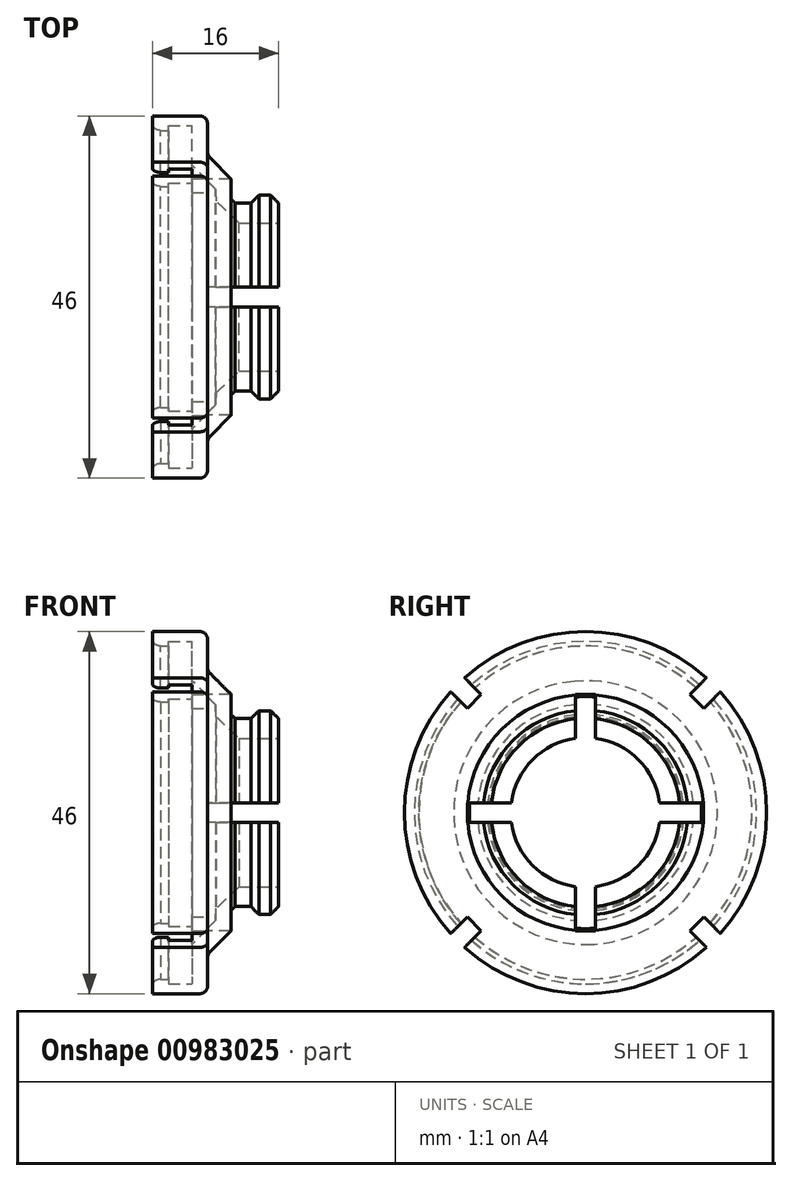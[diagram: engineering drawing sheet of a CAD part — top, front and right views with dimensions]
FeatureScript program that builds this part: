
annotation { "Feature Type Name" : "Feature", "Feature Type Description" : "" }
export const myFeature = defineFeature(function(context is Context, id is Id, definition is map)
    precondition{}
    {
        {
            var Q0;
            Q0=qCreatedBy(makeId("Front.planeOp"),FACE);
            var sketch = newSketch(context, id + "F0", { "sketchPlane" : qUnion([Q0])});
            skLineSegment(sketch, "E0", {"start": v(0, 0) * mm, "end": v(-33.83, 0) * mm, "construction": true});
            skLineSegment(sketch, "E1", {"start": v(-7, 21.75) * mm, "end": v(-5, 21.75) * mm});
            skLineSegment(sketch, "E2", {"start": v(-5, 21.75) * mm, "end": v(-5, 21.75) * mm});
            skLineSegment(sketch, "E3", {"start": v(-5, 21.75) * mm, "end": v(-2, 21.75) * mm});
            skLineSegment(sketch, "E4", {"start": v(5.5, 12) * mm, "end": v(5.5, 13) * mm});
            skLineSegment(sketch, "E5", {"start": v(-2, 21.75) * mm, "end": v(-2, 16.75) * mm});
            skLineSegment(sketch, "E6", {"start": v(-2, 16.75) * mm, "end": v(1, 13.75) * mm});
            skLineSegment(sketch, "E7", {"start": v(3, 15) * mm, "end": v(0, 18) * mm});
            skLineSegment(sketch, "E8", {"start": v(0, 18) * mm, "end": v(0, 23) * mm});
            skLineSegment(sketch, "E9", {"start": v(-7, 23) * mm, "end": v(-7, 21.75) * mm});
            skLineSegment(sketch, "E10", {"start": v(9, 9.5) * mm, "end": v(4, 9.5) * mm});
            skLineSegment(sketch, "E11", {"start": v(1.06, 12.25) * mm, "end": v(1, 13.75) * mm});
            skArc(sketch, "E12", {"start": v(-7, 21.75) * mm, "mid": v(-6, 21.17) * mm, "end": v(-5, 21.75) * mm});
            skLineSegment(sketch, "E13", {"start": v(-7, 23) * mm, "end": v(0, 23) * mm});
            skLineSegment(sketch, "E14", {"start": v(1.06, 12.25) * mm, "end": v(4, 9.5) * mm});
            skLineSegment(sketch, "E15.bottom", {"start": v(-6, 21.75) * mm, "end": v(-5, 21.75) * mm});
            skLineSegment(sketch, "E15.top", {"start": v(-6, 21.17) * mm, "end": v(-5, 21.17) * mm});
            skLineSegment(sketch, "E15.left", {"start": v(-6, 21.75) * mm, "end": v(-6, 21.17) * mm});
            skLineSegment(sketch, "E15.right", {"start": v(-5, 21.75) * mm, "end": v(-5, 21.17) * mm});
            skLineSegment(sketch, "E16", {"start": v(5.5, 13) * mm, "end": v(9, 13) * mm});
            skLineSegment(sketch, "E17", {"start": v(5.5, 12) * mm, "end": v(3.5, 12) * mm});
            skLineSegment(sketch, "E18", {"start": v(3, 15) * mm, "end": v(3, 12.5) * mm});
            skLineSegment(sketch, "E19", {"start": v(3, 12.5) * mm, "end": v(3.5, 12) * mm});
            skLineSegment(sketch, "E20", {"start": v(9, 13) * mm, "end": v(9, 9.5) * mm});
            skSolve(sketch);
        }
        {
            var Q0;
            Q0=qCreatedBy(makeId("Right.planeOp"),FACE);
            var sketch = newSketch(context, id + "F1", { "sketchPlane" : qUnion([Q0])});
            skLineSegment(sketch, "E21.bottom", {"start": v(-1.25, 15) * mm, "end": v(1.25, 15) * mm});
            skLineSegment(sketch, "E21.top", {"start": v(-1.25, -15) * mm, "end": v(1.25, -15) * mm});
            skLineSegment(sketch, "E21.left", {"start": v(-1.25, 15) * mm, "end": v(-1.25, -15) * mm});
            skLineSegment(sketch, "E21.right", {"start": v(1.25, 15) * mm, "end": v(1.25, -15) * mm});
            skSolve(sketch);
        }
        {
            var Q0;
            Q0=qCreatedBy(makeId("Right.planeOp"),FACE);
            var sketch = newSketch(context, id + "F2", { "sketchPlane" : qUnion([Q0])});
            skLineSegment(sketch, "E22.bottom", {"start": v(-15, 1.25) * mm, "end": v(15, 1.25) * mm});
            skLineSegment(sketch, "E22.top", {"start": v(-15, -1.25) * mm, "end": v(15, -1.25) * mm});
            skLineSegment(sketch, "E22.left", {"start": v(-15, 1.25) * mm, "end": v(-15, -1.25) * mm});
            skLineSegment(sketch, "E22.right", {"start": v(15, 1.25) * mm, "end": v(15, -1.25) * mm});
            skSolve(sketch);
        }
        {
            var Q0;
            Q0 = qSketchRegion(id + "F0", true);
            var Q1;
            Q1=sQuery(id+"F0.wireOp",EDGE,"E0");
            revolve(context, id + "F3", {"surfaceOperationType" : NewSurfaceOperationType.NEW, "entities" : qUnion([Q0]), "axis" : qUnion([Q1]), "revolveType" : RevolveType.FULL});
        }
        {
            var Q0;
            Q0 = qSketchRegion(id + "F1", true);
            extrude(context, id + "F4", {"entities" : qUnion([Q0]), "operationType" : NewBodyOperationType.REMOVE, "depth" : 20 * mm, "offsetDistance" : 25 * mm});
        }
        {
            var Q0;
            Q0 = qSketchRegion(id + "F2", true);
            extrude(context, id + "F5", {"entities" : qUnion([Q0]), "operationType" : NewBodyOperationType.REMOVE, "depth" : 20 * mm, "offsetDistance" : 25 * mm});
        }
        {
            var Q0;
            Q0=makeQuery(id+"F3.opRevolve","SWEPT_EDGE",EDGE,{"disambiguationData":[OSD([sQuery(id+"F0.wireOp",EDGE,"AhvpBqBA-tZ8w-fHzy-bnX2-0eLYJSzQ2YSn"),sQuery(id+"F0.wireOp",EDGE,"E8")])]});
            fillet(context, id + "F6", {"entities" : qUnion([Q0]), "radius" : 1 * mm, "tangentPropagation" : true, "allowEdgeOverflow" : false});
        }
        {
            var Q0;
            Q0=qCreatedBy(makeId("Right.planeOp"),FACE);
            var sketch = newSketch(context, id + "F7", { "sketchPlane" : qUnion([Q0])});
            skLineSegment(sketch, "E23.bottom", {"start": v(-16.8, 18.56) * mm, "end": v(-13.26, 15.03) * mm});
            skLineSegment(sketch, "E23.top", {"start": v(-18.56, 16.8) * mm, "end": v(-15.03, 13.26) * mm});
            skLineSegment(sketch, "E23.left", {"start": v(-16.8, 18.56) * mm, "end": v(-18.56, 16.8) * mm});
            skLineSegment(sketch, "E23.right", {"start": v(-13.26, 15.03) * mm, "end": v(-15.03, 13.26) * mm});
            skPoint(sketch, "E23.middle", {"position": v(-22.5, 0) * mm});
            skLineSegment(sketch, "E24.0", {"start": v(-16.8, 18.56) * mm, "end": v(-13.26, 15.03) * mm, "construction": true});
            skLineSegment(sketch, "E24.1", {"start": v(-16.8, 18.56) * mm, "end": v(-16.8, 18.56) * mm});
            skLineSegment(sketch, "E24.8", {"start": v(-18.56, 16.8) * mm, "end": v(-18.56, 16.8) * mm});
            skLineSegment(sketch, "E24.9", {"start": v(-18.56, 16.8) * mm, "end": v(-16.8, 18.56) * mm, "construction": true});
            skLineSegment(sketch, "E25.1.0", {"start": v(16.8, 18.56) * mm, "end": v(13.26, 15.03) * mm});
            skLineSegment(sketch, "E25.1.1", {"start": v(15.03, 13.26) * mm, "end": v(13.26, 15.03) * mm});
            skLineSegment(sketch, "E25.1.2", {"start": v(18.56, 16.8) * mm, "end": v(15.03, 13.26) * mm});
            skLineSegment(sketch, "E25.1.3", {"start": v(16.8, 18.56) * mm, "end": v(18.56, 16.8) * mm});
            skLineSegment(sketch, "E25.2.0", {"start": v(18.56, -16.8) * mm, "end": v(15.03, -13.26) * mm});
            skLineSegment(sketch, "E25.2.1", {"start": v(13.26, -15.03) * mm, "end": v(15.03, -13.26) * mm});
            skLineSegment(sketch, "E25.2.2", {"start": v(16.8, -18.56) * mm, "end": v(13.26, -15.03) * mm});
            skLineSegment(sketch, "E25.2.3", {"start": v(18.56, -16.8) * mm, "end": v(16.8, -18.56) * mm});
            skLineSegment(sketch, "E25.3.0", {"start": v(-16.8, -18.56) * mm, "end": v(-13.26, -15.03) * mm});
            skLineSegment(sketch, "E25.3.1", {"start": v(-15.03, -13.26) * mm, "end": v(-13.26, -15.03) * mm});
            skLineSegment(sketch, "E25.3.2", {"start": v(-18.56, -16.8) * mm, "end": v(-15.03, -13.26) * mm});
            skLineSegment(sketch, "E25.3.3", {"start": v(-16.8, -18.56) * mm, "end": v(-18.56, -16.8) * mm});
            skPoint(sketch, "E25.center", {"position": v(0, 0) * mm});
            skLineSegment(sketch, "E25.anchor1", {"start": v(0, 0) * mm, "end": v(-15.03, 13.26) * mm, "construction": true});
            skLineSegment(sketch, "E25.anchor2", {"start": v(0, 0) * mm, "end": v(-13.26, -15.03) * mm, "construction": true});
            skLineSegment(sketch, "E26", {"start": v(-13.26, -15.03) * mm, "end": v(-15.03, -13.26) * mm});
            skLineSegment(sketch, "E27", {"start": v(-18.56, -16.8) * mm, "end": v(-16.8, -18.56) * mm});
            skSolve(sketch);
        }
        {
            var Q0;
            Q0=makeQuery(id+"F7.imprint","IMPRINT",FACE,{"disambiguationData":[TD([[makeQuery(id+"F7.imprint","IMPRINT",EDGE,{"derivedFrom":sQuery(id+"F7.wireOp",EDGE,"E23.bottom")}),-1.0]])]});
            var Q1;
            Q1=makeQuery(id+"F7.imprint","IMPRINT",FACE,{"disambiguationData":[TD([[makeQuery(id+"F7.imprint","IMPRINT",EDGE,{"derivedFrom":sQuery(id+"F7.wireOp",EDGE,"E25.1.0")}),1.0]])]});
            var Q2;
            Q2=makeQuery(id+"F7.imprint","IMPRINT",FACE,{"disambiguationData":[TD([[makeQuery(id+"F7.imprint","IMPRINT",EDGE,{"derivedFrom":sQuery(id+"F7.wireOp",EDGE,"E25.2.0")}),1.0]])]});
            var Q3;
            Q3=makeQuery(id+"F7.imprint","IMPRINT",FACE,{"disambiguationData":[TD([[makeQuery(id+"F7.imprint","IMPRINT",EDGE,{"derivedFrom":sQuery(id+"F7.wireOp",EDGE,"E25.3.0")}),1.0]])]});
            var Q4;
            Q4=sQuery(id+"F7.wireOp",EDGE,"E25.3.0");
            var Q5;
            Q5=sQuery(id+"F7.wireOp",EDGE,"E25.3.2");
            var Q6;
            Q6=sQuery(id+"F7.wireOp",EDGE,"E26");
            var Q7;
            Q7=sQuery(id+"F7.wireOp",EDGE,"E23.top");
            var Q8;
            Q8=sQuery(id+"F7.wireOp",EDGE,"E23.left");
            var Q9;
            Q9=sQuery(id+"F7.wireOp",EDGE,"E23.bottom");
            var Q10;
            Q10=sQuery(id+"F7.wireOp",EDGE,"E23.right");
            var Q11;
            Q11=sQuery(id+"F7.wireOp",EDGE,"E25.1.1");
            var Q12;
            Q12=sQuery(id+"F7.wireOp",EDGE,"E25.1.0");
            var Q13;
            Q13=sQuery(id+"F7.wireOp",EDGE,"E25.1.3");
            var Q14;
            Q14=sQuery(id+"F7.wireOp",EDGE,"E25.1.2");
            var Q15;
            Q15=sQuery(id+"F7.wireOp",EDGE,"E25.2.0");
            var Q16;
            Q16=sQuery(id+"F7.wireOp",EDGE,"E25.2.3");
            var Q17;
            Q17=sQuery(id+"F7.wireOp",EDGE,"E25.2.2");
            var Q18;
            Q18=sQuery(id+"F7.wireOp",EDGE,"E25.2.1");
            extrude(context, id + "F8", {"entities" : qUnion([Q0, Q1, Q2, Q3]), "operationType" : NewBodyOperationType.REMOVE, "surfaceEntities" : qUnion([Q4, Q5, Q6, Q7, Q8, Q9, Q10, Q11, Q12, Q13, Q14, Q15, Q16, Q17, Q18]), "oppositeDirection" : true, "depth" : 13.7 * mm, "offsetDistance" : 25 * mm});
        }
        {
            var Q0;
            {var subQ0=sQuery(id+"F0.wireOp",EDGE,"E4");var subQ2=sQuery(id+"F0.wireOp",EDGE,"E16");var subQ5=sQuery(id+"F1.wireOp",EDGE,"E21.left");var subQ6=makeQuery(id+"F4.opExtrude","SWEPT_FACE",FACE,{"disambiguationData":[OSD([subQ5])]});Q0=makeQuery(id+"F5.boolean.opBoolean","SPLIT",EDGE,{"disambiguationData":[TD([makeQuery(id+"F5.opExtrude","SWEPT_FACE",FACE,{"disambiguationData":[OSD([sQuery(id+"F2.wireOp",EDGE,"E22.bottom")])]})])],"derivedFrom":makeQuery(id+"F4.boolean.opBoolean","SPLIT",EDGE,{"disambiguationData":[TD([subQ6])],"derivedFrom":makeQuery(id+"F3.opRevolve","SWEPT_EDGE",EDGE,{"disambiguationData":[OSD([subQ0,subQ2])]})})});}
            var Q1;
            {var subQ0=sQuery(id+"F0.wireOp",EDGE,"E16");var subQ2=sQuery(id+"F0.wireOp",EDGE,"E20");var subQ5=sQuery(id+"F1.wireOp",EDGE,"E21.left");var subQ6=makeQuery(id+"F4.opExtrude","SWEPT_FACE",FACE,{"disambiguationData":[OSD([subQ5])]});Q1=makeQuery(id+"F5.boolean.opBoolean","SPLIT",EDGE,{"disambiguationData":[TD([makeQuery(id+"F5.opExtrude","SWEPT_FACE",FACE,{"disambiguationData":[OSD([sQuery(id+"F2.wireOp",EDGE,"E22.bottom")])]})])],"derivedFrom":makeQuery(id+"F4.boolean.opBoolean","SPLIT",EDGE,{"disambiguationData":[TD([subQ6])],"derivedFrom":makeQuery(id+"F3.opRevolve","SWEPT_EDGE",EDGE,{"disambiguationData":[OSD([subQ0,subQ2])]})})});}
            var Q2;
            {var subQ0=sQuery(id+"F0.wireOp",EDGE,"E16");var subQ2=sQuery(id+"F0.wireOp",EDGE,"E20");var subQ5=sQuery(id+"F1.wireOp",EDGE,"E21.right");var subQ6=makeQuery(id+"F4.opExtrude","SWEPT_FACE",FACE,{"disambiguationData":[OSD([subQ5])]});Q2=makeQuery(id+"F5.boolean.opBoolean","SPLIT",EDGE,{"disambiguationData":[TD([makeQuery(id+"F5.opExtrude","SWEPT_FACE",FACE,{"disambiguationData":[OSD([sQuery(id+"F2.wireOp",EDGE,"E22.bottom")])]})])],"derivedFrom":makeQuery(id+"F4.boolean.opBoolean","SPLIT",EDGE,{"disambiguationData":[TD([subQ6])],"derivedFrom":makeQuery(id+"F3.opRevolve","SWEPT_EDGE",EDGE,{"disambiguationData":[OSD([subQ0,subQ2])]})})});}
            var Q3;
            {var subQ0=sQuery(id+"F0.wireOp",EDGE,"E16");var subQ2=sQuery(id+"F0.wireOp",EDGE,"E20");var subQ4=sQuery(id+"F1.wireOp",EDGE,"E21.right");var subQ6=makeQuery(id+"F4.opExtrude","SWEPT_FACE",FACE,{"disambiguationData":[OSD([subQ4])]});Q3=makeQuery(id+"F5.boolean.opBoolean","SPLIT",EDGE,{"disambiguationData":[TD([makeQuery(id+"F5.opExtrude","SWEPT_FACE",FACE,{"disambiguationData":[OSD([sQuery(id+"F2.wireOp",EDGE,"E22.top")])]})])],"derivedFrom":makeQuery(id+"F4.boolean.opBoolean","SPLIT",EDGE,{"disambiguationData":[TD([subQ6])],"derivedFrom":makeQuery(id+"F3.opRevolve","SWEPT_EDGE",EDGE,{"disambiguationData":[OSD([subQ0,subQ2])]})})});}
            var Q4;
            {var subQ0=sQuery(id+"F0.wireOp",EDGE,"E16");var subQ2=sQuery(id+"F0.wireOp",EDGE,"E20");var subQ4=sQuery(id+"F1.wireOp",EDGE,"E21.left");var subQ6=makeQuery(id+"F4.opExtrude","SWEPT_FACE",FACE,{"disambiguationData":[OSD([subQ4])]});Q4=makeQuery(id+"F5.boolean.opBoolean","SPLIT",EDGE,{"disambiguationData":[TD([makeQuery(id+"F5.opExtrude","SWEPT_FACE",FACE,{"disambiguationData":[OSD([sQuery(id+"F2.wireOp",EDGE,"E22.top")])]})])],"derivedFrom":makeQuery(id+"F4.boolean.opBoolean","SPLIT",EDGE,{"disambiguationData":[TD([subQ6])],"derivedFrom":makeQuery(id+"F3.opRevolve","SWEPT_EDGE",EDGE,{"disambiguationData":[OSD([subQ0,subQ2])]})})});}
            var Q5;
            {var subQ0=sQuery(id+"F0.wireOp",EDGE,"E4");var subQ2=sQuery(id+"F0.wireOp",EDGE,"E16");var subQ4=sQuery(id+"F1.wireOp",EDGE,"E21.left");var subQ6=makeQuery(id+"F4.opExtrude","SWEPT_FACE",FACE,{"disambiguationData":[OSD([subQ4])]});Q5=makeQuery(id+"F5.boolean.opBoolean","SPLIT",EDGE,{"disambiguationData":[TD([makeQuery(id+"F5.opExtrude","SWEPT_FACE",FACE,{"disambiguationData":[OSD([sQuery(id+"F2.wireOp",EDGE,"E22.top")])]})])],"derivedFrom":makeQuery(id+"F4.boolean.opBoolean","SPLIT",EDGE,{"disambiguationData":[TD([subQ6])],"derivedFrom":makeQuery(id+"F3.opRevolve","SWEPT_EDGE",EDGE,{"disambiguationData":[OSD([subQ0,subQ2])]})})});}
            var Q6;
            {var subQ0=sQuery(id+"F0.wireOp",EDGE,"E4");var subQ2=sQuery(id+"F0.wireOp",EDGE,"E16");var subQ5=sQuery(id+"F1.wireOp",EDGE,"E21.right");var subQ6=makeQuery(id+"F4.opExtrude","SWEPT_FACE",FACE,{"disambiguationData":[OSD([subQ5])]});Q6=makeQuery(id+"F5.boolean.opBoolean","SPLIT",EDGE,{"disambiguationData":[TD([makeQuery(id+"F5.opExtrude","SWEPT_FACE",FACE,{"disambiguationData":[OSD([sQuery(id+"F2.wireOp",EDGE,"E22.bottom")])]})])],"derivedFrom":makeQuery(id+"F4.boolean.opBoolean","SPLIT",EDGE,{"disambiguationData":[TD([subQ6])],"derivedFrom":makeQuery(id+"F3.opRevolve","SWEPT_EDGE",EDGE,{"disambiguationData":[OSD([subQ0,subQ2])]})})});}
            var Q7;
            {var subQ0=sQuery(id+"F0.wireOp",EDGE,"E4");var subQ2=sQuery(id+"F0.wireOp",EDGE,"E16");var subQ4=sQuery(id+"F1.wireOp",EDGE,"E21.right");var subQ6=makeQuery(id+"F4.opExtrude","SWEPT_FACE",FACE,{"disambiguationData":[OSD([subQ4])]});Q7=makeQuery(id+"F5.boolean.opBoolean","SPLIT",EDGE,{"disambiguationData":[TD([makeQuery(id+"F5.opExtrude","SWEPT_FACE",FACE,{"disambiguationData":[OSD([sQuery(id+"F2.wireOp",EDGE,"E22.top")])]})])],"derivedFrom":makeQuery(id+"F4.boolean.opBoolean","SPLIT",EDGE,{"disambiguationData":[TD([subQ6])],"derivedFrom":makeQuery(id+"F3.opRevolve","SWEPT_EDGE",EDGE,{"disambiguationData":[OSD([subQ0,subQ2])]})})});}
            chamfer(context, id + "F9", {"entities" : qUnion([Q0, Q1, Q2, Q3, Q4, Q5, Q6, Q7]), "width" : 1 * mm, "tangentPropagation" : true});
        }
    });
